# Revit family: Escutcheon-Lixil-Grohe_Cubeo_for_Single_Hole_Faucets_105378
name_source: partatom
category: Plumbing Fixtures
units: mm (PartAtom-declared; Revit-internal decimal feet)

## family parameters
Cut with Voids When Loaded = No
Enable Cutting in Views = No
Host = Face
Maintain Annotation Orientation = No
OmniClass Number = 23.45.05.14.17
OmniClass Title = Showers
Part Type = Normal
Room Calculation Point = No
Round Connector Dimension = Use Diameter
Shared = No

## types (4) — shared parameters
Assembly Code = D2010700
Brand = Grohe
CW Connection = No
Collection = Cubeo
Default Elevation = 0' - 0"
Description = Escutcheon
Flow Rate = 0 GPM
HW Connection = No
Keynote = 22 41 39
Manufacturer = LIXIL
Material = Solid Brass Body Construction
Product Documentation Link = https://lixil.cdn.celum.cloud
Product Name = Cubeo Escutcheon for Single Hole Faucets
Product Page URL = https://lixilpro.com
URL = https://www.grohe.com
Vent Connection = No
Version = 2023 v.1.0a
Warranty URL = Contact Manufacturer for More Information
Waste Connection = No
zero-valued in all types: CWFU, HWFU, WFU

## per-type parameters (varying)
| type | Finish | Model |
| Chrome | Metal - Grohe - Chrome | 1053780000 |
| Matte Black | Metal - Grohe - Matte Black | 1053782430 |
| Brushed Nickel | Metal - Grohe - Brushed Nickel | 105378EN00 |
| Brushed Cool Sunrise | Metal - Grohe - Brushed Cool Sunrise | 105378GN00 |

## geometry (parser evidence)
native form markers: Sweep x2
no freeform markers — native parametric forms only
